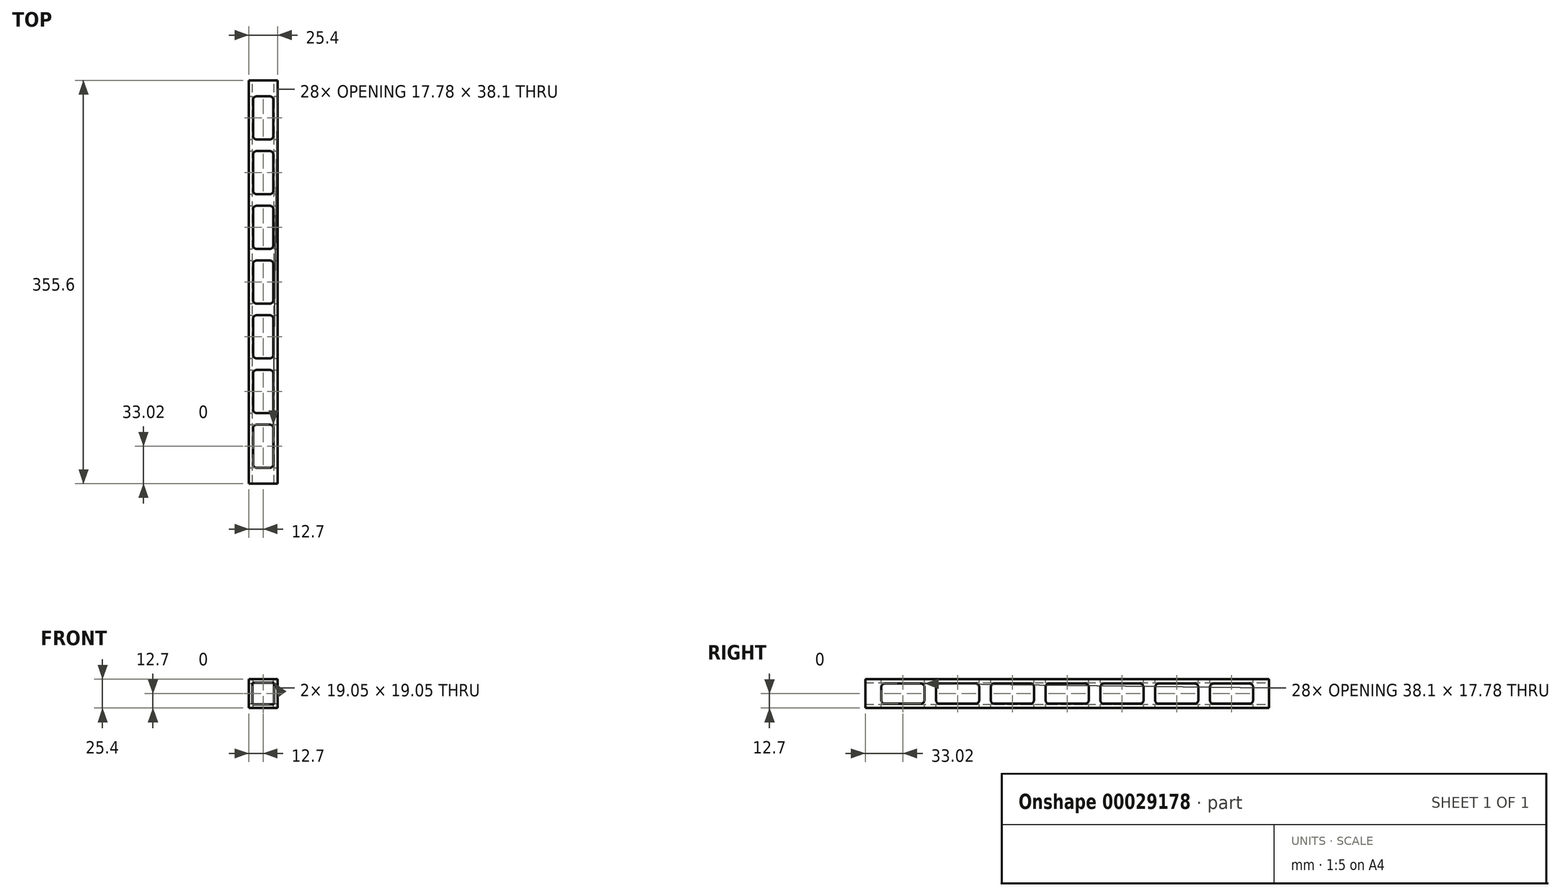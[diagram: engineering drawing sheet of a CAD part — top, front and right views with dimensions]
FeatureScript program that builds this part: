
annotation { "Feature Type Name" : "Feature", "Feature Type Description" : "" }
export const myFeature = defineFeature(function(context is Context, id is Id, definition is map)
    precondition{}
    {
        {
            var Q0;
            Q0=qCreatedBy(makeId("Front.planeOp"),FACE);
            var sketch = newSketch(context, id + "F0", { "sketchPlane" : qUnion([Q0])});
            skLineSegment(sketch, "E0.rect.bottom", {"start": v(12.7, 12.7) * mm, "end": v(-12.7, 12.7) * mm});
            skLineSegment(sketch, "E0.rect.top", {"start": v(12.7, -12.7) * mm, "end": v(-12.7, -12.7) * mm});
            skLineSegment(sketch, "E0.rect.left", {"start": v(12.7, 12.7) * mm, "end": v(12.7, -12.7) * mm});
            skLineSegment(sketch, "E0.rect.right", {"start": v(-12.7, 12.7) * mm, "end": v(-12.7, -12.7) * mm});
            skPoint(sketch, "E0.rect.middle", {"position": v(0, 0) * mm});
            skLineSegment(sketch, "E1.rect.bottom", {"start": v(9.53, 9.53) * mm, "end": v(-9.53, 9.53) * mm});
            skLineSegment(sketch, "E1.rect.top", {"start": v(9.53, -9.53) * mm, "end": v(-9.53, -9.53) * mm});
            skLineSegment(sketch, "E1.rect.left", {"start": v(9.53, 9.53) * mm, "end": v(9.53, -9.53) * mm});
            skLineSegment(sketch, "E1.rect.right", {"start": v(-9.53, 9.53) * mm, "end": v(-9.53, -9.53) * mm});
            skSolve(sketch);
        }
        {
            var Q0;
            Q0=qSketchRegion(id+"F0",true);
            extrude(context, id + "F1", {"entities" : qUnion([Q0]), "depth" : 355.6 * mm});
        }
        {
            var Q0;
            Q0=makeQuery(id+"F1.opExtrude","SWEPT_FACE",FACE,{"disambiguationData":[OSD([sQuery(id+"F0.wireOp",EDGE,"E0.rect.left")])]});
            var sketch = newSketch(context, id + "F2", { "sketchPlane" : qUnion([Q0])});
            skLineSegment(sketch, "E2", {"start": v(-355.6, 0) * mm, "end": v(-341.63, 0) * mm});
            skLineSegment(sketch, "E3.rect.bottom", {"start": v(-306.7, 8.89) * mm, "end": v(-338.46, 8.89) * mm});
            skLineSegment(sketch, "E3.rect.top", {"start": v(-306.7, -8.9) * mm, "end": v(-338.46, -8.9) * mm});
            skLineSegment(sketch, "E3.rect.left", {"start": v(-303.53, 5.71) * mm, "end": v(-303.53, -5.72) * mm});
            skLineSegment(sketch, "E3.rect.right", {"start": v(-341.63, 5.71) * mm, "end": v(-341.63, -5.72) * mm});
            skPoint(sketch, "E3.rect.middle", {"position": v(-322.58, 0) * mm});
            skPoint(sketch, "E4.visualSharp", {"position": v(-303.53, 8.89) * mm});
            skArc(sketch, "E4.filletArc", {"start": v(-303.53, 5.71) * mm, "mid": v(-304.46, 7.96) * mm, "end": v(-306.7, 8.89) * mm});
            skPoint(sketch, "E5.visualSharp", {"position": v(-303.53, -8.9) * mm});
            skArc(sketch, "E5.filletArc", {"start": v(-306.7, -8.9) * mm, "mid": v(-304.46, -7.96) * mm, "end": v(-303.53, -5.72) * mm});
            skPoint(sketch, "E6.visualSharp", {"position": v(-341.63, -8.9) * mm});
            skArc(sketch, "E6.filletArc", {"start": v(-341.63, -5.72) * mm, "mid": v(-340.7, -7.96) * mm, "end": v(-338.46, -8.9) * mm});
            skPoint(sketch, "E7.visualSharp", {"position": v(-341.63, 8.89) * mm});
            skArc(sketch, "E7.filletArc", {"start": v(-338.46, 8.89) * mm, "mid": v(-340.7, 7.96) * mm, "end": v(-341.63, 5.71) * mm});
            skLineSegment(sketch, "E8.1.0.0", {"start": v(-255.27, 5.71) * mm, "end": v(-255.27, -5.72) * mm});
            skArc(sketch, "E8.1.0.1", {"start": v(-255.27, 5.71) * mm, "mid": v(-256.2, 7.96) * mm, "end": v(-258.44, 8.89) * mm});
            skLineSegment(sketch, "E8.1.0.2", {"start": v(-258.44, 8.89) * mm, "end": v(-290.2, 8.89) * mm});
            skArc(sketch, "E8.1.0.3", {"start": v(-290.2, 8.89) * mm, "mid": v(-292.44, 7.96) * mm, "end": v(-293.37, 5.71) * mm});
            skLineSegment(sketch, "E8.1.0.4", {"start": v(-293.37, 5.71) * mm, "end": v(-293.37, -5.72) * mm});
            skArc(sketch, "E8.1.0.5", {"start": v(-293.37, -5.72) * mm, "mid": v(-292.44, -7.96) * mm, "end": v(-290.2, -8.9) * mm});
            skLineSegment(sketch, "E8.1.0.6", {"start": v(-258.44, -8.9) * mm, "end": v(-290.2, -8.9) * mm});
            skLineSegment(sketch, "E8.2.0.0", {"start": v(-207, 5.71) * mm, "end": v(-207, -5.72) * mm});
            skArc(sketch, "E8.2.0.1", {"start": v(-207, 5.71) * mm, "mid": v(-207.94, 7.96) * mm, "end": v(-210.18, 8.89) * mm});
            skLineSegment(sketch, "E8.2.0.2", {"start": v(-210.18, 8.89) * mm, "end": v(-241.94, 8.89) * mm});
            skArc(sketch, "E8.2.0.3", {"start": v(-241.94, 8.89) * mm, "mid": v(-244.18, 7.96) * mm, "end": v(-245.1, 5.71) * mm});
            skLineSegment(sketch, "E8.2.0.4", {"start": v(-245.1, 5.71) * mm, "end": v(-245.1, -5.72) * mm});
            skArc(sketch, "E8.2.0.5", {"start": v(-245.1, -5.72) * mm, "mid": v(-244.18, -7.96) * mm, "end": v(-241.94, -8.9) * mm});
            skLineSegment(sketch, "E8.2.0.6", {"start": v(-210.18, -8.9) * mm, "end": v(-241.94, -8.9) * mm});
            skLineSegment(sketch, "E8.3.0.0", {"start": v(-158.75, 5.71) * mm, "end": v(-158.75, -5.72) * mm});
            skArc(sketch, "E8.3.0.1", {"start": v(-158.75, 5.71) * mm, "mid": v(-159.68, 7.96) * mm, "end": v(-161.92, 8.89) * mm});
            skLineSegment(sketch, "E8.3.0.2", {"start": v(-161.92, 8.89) * mm, "end": v(-193.67, 8.89) * mm});
            skArc(sketch, "E8.3.0.3", {"start": v(-193.67, 8.89) * mm, "mid": v(-195.92, 7.96) * mm, "end": v(-196.85, 5.71) * mm});
            skLineSegment(sketch, "E8.3.0.4", {"start": v(-196.85, 5.71) * mm, "end": v(-196.85, -5.72) * mm});
            skArc(sketch, "E8.3.0.5", {"start": v(-196.85, -5.72) * mm, "mid": v(-195.92, -7.96) * mm, "end": v(-193.67, -8.9) * mm});
            skLineSegment(sketch, "E8.3.0.6", {"start": v(-161.92, -8.9) * mm, "end": v(-193.67, -8.9) * mm});
            skLineSegment(sketch, "E8.4.0.0", {"start": v(-110.49, 5.71) * mm, "end": v(-110.49, -5.72) * mm});
            skArc(sketch, "E8.4.0.1", {"start": v(-110.49, 5.71) * mm, "mid": v(-111.42, 7.96) * mm, "end": v(-113.66, 8.89) * mm});
            skLineSegment(sketch, "E8.4.0.2", {"start": v(-113.66, 8.89) * mm, "end": v(-145.41, 8.89) * mm});
            skArc(sketch, "E8.4.0.3", {"start": v(-145.41, 8.89) * mm, "mid": v(-147.66, 7.96) * mm, "end": v(-148.59, 5.71) * mm});
            skLineSegment(sketch, "E8.4.0.4", {"start": v(-148.59, 5.71) * mm, "end": v(-148.59, -5.72) * mm});
            skArc(sketch, "E8.4.0.5", {"start": v(-148.59, -5.72) * mm, "mid": v(-147.66, -7.96) * mm, "end": v(-145.41, -8.9) * mm});
            skLineSegment(sketch, "E8.4.0.6", {"start": v(-113.66, -8.9) * mm, "end": v(-145.41, -8.9) * mm});
            skLineSegment(sketch, "E8.5.0.0", {"start": v(-62.23, 5.71) * mm, "end": v(-62.23, -5.72) * mm});
            skArc(sketch, "E8.5.0.1", {"start": v(-62.23, 5.71) * mm, "mid": v(-63.16, 7.96) * mm, "end": v(-65.4, 8.89) * mm});
            skLineSegment(sketch, "E8.5.0.2", {"start": v(-65.4, 8.89) * mm, "end": v(-97.15, 8.89) * mm});
            skArc(sketch, "E8.5.0.3", {"start": v(-97.15, 8.89) * mm, "mid": v(-99.4, 7.96) * mm, "end": v(-100.33, 5.71) * mm});
            skLineSegment(sketch, "E8.5.0.4", {"start": v(-100.33, 5.71) * mm, "end": v(-100.33, -5.72) * mm});
            skArc(sketch, "E8.5.0.5", {"start": v(-100.33, -5.72) * mm, "mid": v(-99.4, -7.96) * mm, "end": v(-97.15, -8.9) * mm});
            skLineSegment(sketch, "E8.5.0.6", {"start": v(-65.4, -8.9) * mm, "end": v(-97.15, -8.9) * mm});
            skLineSegment(sketch, "E8.6.0.0", {"start": v(-13.97, 5.71) * mm, "end": v(-13.97, -5.72) * mm});
            skArc(sketch, "E8.6.0.1", {"start": v(-13.97, 5.71) * mm, "mid": v(-14.9, 7.96) * mm, "end": v(-17.14, 8.89) * mm});
            skLineSegment(sketch, "E8.6.0.2", {"start": v(-17.14, 8.89) * mm, "end": v(-48.9, 8.89) * mm});
            skArc(sketch, "E8.6.0.3", {"start": v(-48.9, 8.89) * mm, "mid": v(-51.14, 7.96) * mm, "end": v(-52.07, 5.71) * mm});
            skLineSegment(sketch, "E8.6.0.4", {"start": v(-52.07, 5.71) * mm, "end": v(-52.07, -5.72) * mm});
            skArc(sketch, "E8.6.0.5", {"start": v(-52.07, -5.72) * mm, "mid": v(-51.14, -7.96) * mm, "end": v(-48.9, -8.9) * mm});
            skLineSegment(sketch, "E8.6.0.6", {"start": v(-17.14, -8.9) * mm, "end": v(-48.9, -8.9) * mm});
            skLineSegment(sketch, "E8.direction1", {"start": v(-303.53, -5.72) * mm, "end": v(-255.27, -5.72) * mm, "construction": true});
            skLineSegment(sketch, "E9.trimOffspring", {"start": v(-303.53, 0) * mm, "end": v(-293.37, 0) * mm});
            skLineSegment(sketch, "E10.trimOffspring", {"start": v(-255.27, 0) * mm, "end": v(0, 0) * mm});
            skArc(sketch, "E11.1.0.0", {"start": v(-258.44, -8.9) * mm, "mid": v(-256.2, -7.96) * mm, "end": v(-255.27, -5.72) * mm});
            skArc(sketch, "E11.2.0.0", {"start": v(-210.18, -8.9) * mm, "mid": v(-207.94, -7.96) * mm, "end": v(-207, -5.72) * mm});
            skArc(sketch, "E11.3.0.0", {"start": v(-161.92, -8.9) * mm, "mid": v(-159.68, -7.96) * mm, "end": v(-158.75, -5.72) * mm});
            skArc(sketch, "E11.4.0.0", {"start": v(-113.66, -8.9) * mm, "mid": v(-111.42, -7.96) * mm, "end": v(-110.49, -5.72) * mm});
            skArc(sketch, "E11.5.0.0", {"start": v(-65.4, -8.9) * mm, "mid": v(-63.16, -7.96) * mm, "end": v(-62.23, -5.72) * mm});
            skArc(sketch, "E11.6.0.0", {"start": v(-17.14, -8.9) * mm, "mid": v(-14.9, -7.96) * mm, "end": v(-13.97, -5.72) * mm});
            skLineSegment(sketch, "E11.direction1", {"start": v(-306.7, -8.9) * mm, "end": v(-258.44, -8.9) * mm, "construction": true});
            skSolve(sketch);
        }
        {
            var Q0;
            Q0 = qSketchRegion(id + "F2", true);
            extrude(context, id + "F3", {"entities" : qUnion([Q0]), "operationType" : NewBodyOperationType.REMOVE, "oppositeDirection" : true, "depth" : 25.4 * mm});
        }
        {
            var Q0;
            Q0=makeQuery(id+"F1.opExtrude","SWEPT_FACE",FACE,{"disambiguationData":[OSD([sQuery(id+"F0.wireOp",EDGE,"E0.rect.bottom")])]});
            var sketch = newSketch(context, id + "F4", { "sketchPlane" : qUnion([Q0])});
            skLineSegment(sketch, "E12", {"start": v(0, -355.6) * mm, "end": v(0, -341.63) * mm});
            skLineSegment(sketch, "E13.rect.bottom", {"start": v(5.72, -303.53) * mm, "end": v(-5.71, -303.53) * mm});
            skLineSegment(sketch, "E13.rect.top", {"start": v(5.72, -341.63) * mm, "end": v(-5.71, -341.63) * mm});
            skLineSegment(sketch, "E13.rect.left", {"start": v(8.9, -306.7) * mm, "end": v(8.9, -338.46) * mm});
            skLineSegment(sketch, "E13.rect.right", {"start": v(-8.89, -306.7) * mm, "end": v(-8.89, -338.46) * mm});
            skPoint(sketch, "E13.rect.middle", {"position": v(0, -322.58) * mm});
            skPoint(sketch, "E14.visualSharp", {"position": v(-8.89, -303.53) * mm});
            skArc(sketch, "E14.filletArc", {"start": v(-5.71, -303.53) * mm, "mid": v(-7.96, -304.46) * mm, "end": v(-8.89, -306.7) * mm});
            skPoint(sketch, "E15.visualSharp", {"position": v(8.9, -303.53) * mm});
            skArc(sketch, "E15.filletArc", {"start": v(8.9, -306.7) * mm, "mid": v(7.96, -304.46) * mm, "end": v(5.72, -303.53) * mm});
            skPoint(sketch, "E16.visualSharp", {"position": v(8.9, -341.63) * mm});
            skArc(sketch, "E16.filletArc", {"start": v(5.72, -341.63) * mm, "mid": v(7.96, -340.7) * mm, "end": v(8.9, -338.46) * mm});
            skPoint(sketch, "E17.visualSharp", {"position": v(-8.89, -341.63) * mm});
            skArc(sketch, "E17.filletArc", {"start": v(-8.89, -338.46) * mm, "mid": v(-7.96, -340.7) * mm, "end": v(-5.71, -341.63) * mm});
            skLineSegment(sketch, "E18.trimOffspring", {"start": v(0, -303.53) * mm, "end": v(0, 0) * mm});
            skLineSegment(sketch, "E19.0.1.0", {"start": v(5.72, -255.27) * mm, "end": v(-5.71, -255.27) * mm});
            skArc(sketch, "E19.0.1.1", {"start": v(-5.71, -255.27) * mm, "mid": v(-7.96, -256.2) * mm, "end": v(-8.89, -258.44) * mm});
            skLineSegment(sketch, "E19.0.1.2", {"start": v(-8.89, -258.44) * mm, "end": v(-8.89, -290.2) * mm});
            skArc(sketch, "E19.0.1.3", {"start": v(-8.89, -290.2) * mm, "mid": v(-7.96, -292.44) * mm, "end": v(-5.71, -293.37) * mm});
            skLineSegment(sketch, "E19.0.1.4", {"start": v(5.72, -293.37) * mm, "end": v(-5.71, -293.37) * mm});
            skArc(sketch, "E19.0.1.5", {"start": v(5.72, -293.37) * mm, "mid": v(7.96, -292.44) * mm, "end": v(8.9, -290.2) * mm});
            skLineSegment(sketch, "E19.0.1.6", {"start": v(8.9, -258.44) * mm, "end": v(8.9, -290.2) * mm});
            skArc(sketch, "E19.0.1.7", {"start": v(8.9, -258.44) * mm, "mid": v(7.96, -256.2) * mm, "end": v(5.72, -255.27) * mm});
            skLineSegment(sketch, "E19.0.2.0", {"start": v(5.72, -207) * mm, "end": v(-5.71, -207) * mm});
            skArc(sketch, "E19.0.2.1", {"start": v(-5.71, -207) * mm, "mid": v(-7.96, -207.94) * mm, "end": v(-8.89, -210.18) * mm});
            skLineSegment(sketch, "E19.0.2.2", {"start": v(-8.89, -210.18) * mm, "end": v(-8.89, -241.94) * mm});
            skArc(sketch, "E19.0.2.3", {"start": v(-8.89, -241.94) * mm, "mid": v(-7.96, -244.18) * mm, "end": v(-5.71, -245.11) * mm});
            skLineSegment(sketch, "E19.0.2.4", {"start": v(5.72, -245.11) * mm, "end": v(-5.71, -245.11) * mm});
            skArc(sketch, "E19.0.2.5", {"start": v(5.72, -245.11) * mm, "mid": v(7.96, -244.18) * mm, "end": v(8.9, -241.94) * mm});
            skLineSegment(sketch, "E19.0.2.6", {"start": v(8.9, -210.18) * mm, "end": v(8.9, -241.94) * mm});
            skArc(sketch, "E19.0.2.7", {"start": v(8.9, -210.18) * mm, "mid": v(7.96, -207.94) * mm, "end": v(5.72, -207) * mm});
            skLineSegment(sketch, "E19.0.3.0", {"start": v(5.72, -158.75) * mm, "end": v(-5.71, -158.75) * mm});
            skArc(sketch, "E19.0.3.1", {"start": v(-5.71, -158.75) * mm, "mid": v(-7.96, -159.68) * mm, "end": v(-8.89, -161.92) * mm});
            skLineSegment(sketch, "E19.0.3.2", {"start": v(-8.89, -161.92) * mm, "end": v(-8.89, -193.68) * mm});
            skArc(sketch, "E19.0.3.3", {"start": v(-8.89, -193.68) * mm, "mid": v(-7.96, -195.92) * mm, "end": v(-5.71, -196.85) * mm});
            skLineSegment(sketch, "E19.0.3.4", {"start": v(5.72, -196.85) * mm, "end": v(-5.71, -196.85) * mm});
            skArc(sketch, "E19.0.3.5", {"start": v(5.72, -196.85) * mm, "mid": v(7.96, -195.92) * mm, "end": v(8.9, -193.68) * mm});
            skLineSegment(sketch, "E19.0.3.6", {"start": v(8.9, -161.92) * mm, "end": v(8.9, -193.68) * mm});
            skArc(sketch, "E19.0.3.7", {"start": v(8.9, -161.92) * mm, "mid": v(7.96, -159.68) * mm, "end": v(5.72, -158.75) * mm});
            skLineSegment(sketch, "E19.0.4.0", {"start": v(5.72, -110.49) * mm, "end": v(-5.71, -110.49) * mm});
            skArc(sketch, "E19.0.4.1", {"start": v(-5.71, -110.49) * mm, "mid": v(-7.96, -111.42) * mm, "end": v(-8.89, -113.66) * mm});
            skLineSegment(sketch, "E19.0.4.2", {"start": v(-8.89, -113.66) * mm, "end": v(-8.89, -145.42) * mm});
            skArc(sketch, "E19.0.4.3", {"start": v(-8.89, -145.42) * mm, "mid": v(-7.96, -147.66) * mm, "end": v(-5.71, -148.6) * mm});
            skLineSegment(sketch, "E19.0.4.4", {"start": v(5.72, -148.6) * mm, "end": v(-5.71, -148.6) * mm});
            skArc(sketch, "E19.0.4.5", {"start": v(5.72, -148.6) * mm, "mid": v(7.96, -147.66) * mm, "end": v(8.9, -145.42) * mm});
            skLineSegment(sketch, "E19.0.4.6", {"start": v(8.9, -113.66) * mm, "end": v(8.9, -145.42) * mm});
            skArc(sketch, "E19.0.4.7", {"start": v(8.9, -113.66) * mm, "mid": v(7.96, -111.42) * mm, "end": v(5.72, -110.49) * mm});
            skLineSegment(sketch, "E19.0.5.0", {"start": v(5.72, -62.23) * mm, "end": v(-5.71, -62.23) * mm});
            skArc(sketch, "E19.0.5.1", {"start": v(-5.71, -62.23) * mm, "mid": v(-7.96, -63.16) * mm, "end": v(-8.89, -65.4) * mm});
            skLineSegment(sketch, "E19.0.5.2", {"start": v(-8.89, -65.4) * mm, "end": v(-8.89, -97.15) * mm});
            skArc(sketch, "E19.0.5.3", {"start": v(-8.89, -97.15) * mm, "mid": v(-7.96, -99.4) * mm, "end": v(-5.71, -100.33) * mm});
            skLineSegment(sketch, "E19.0.5.4", {"start": v(5.72, -100.33) * mm, "end": v(-5.71, -100.33) * mm});
            skArc(sketch, "E19.0.5.5", {"start": v(5.72, -100.33) * mm, "mid": v(7.96, -99.4) * mm, "end": v(8.9, -97.15) * mm});
            skLineSegment(sketch, "E19.0.5.6", {"start": v(8.9, -65.4) * mm, "end": v(8.9, -97.15) * mm});
            skArc(sketch, "E19.0.5.7", {"start": v(8.9, -65.4) * mm, "mid": v(7.96, -63.16) * mm, "end": v(5.72, -62.23) * mm});
            skLineSegment(sketch, "E19.0.6.0", {"start": v(5.71, -13.97) * mm, "end": v(-5.72, -13.97) * mm});
            skArc(sketch, "E19.0.6.1", {"start": v(-5.72, -13.97) * mm, "mid": v(-7.96, -14.9) * mm, "end": v(-8.89, -17.14) * mm});
            skLineSegment(sketch, "E19.0.6.2", {"start": v(-8.89, -17.14) * mm, "end": v(-8.89, -48.9) * mm});
            skArc(sketch, "E19.0.6.3", {"start": v(-8.89, -48.9) * mm, "mid": v(-7.96, -51.14) * mm, "end": v(-5.72, -52.07) * mm});
            skLineSegment(sketch, "E19.0.6.4", {"start": v(5.71, -52.07) * mm, "end": v(-5.72, -52.07) * mm});
            skArc(sketch, "E19.0.6.5", {"start": v(5.71, -52.07) * mm, "mid": v(7.96, -51.14) * mm, "end": v(8.9, -48.9) * mm});
            skLineSegment(sketch, "E19.0.6.6", {"start": v(8.9, -17.14) * mm, "end": v(8.9, -48.9) * mm});
            skArc(sketch, "E19.0.6.7", {"start": v(8.9, -17.14) * mm, "mid": v(7.96, -14.9) * mm, "end": v(5.71, -13.97) * mm});
            skLineSegment(sketch, "E19.direction1", {"start": v(-5.71, -303.53) * mm, "end": v(19.69, -303.53) * mm, "construction": true});
            skLineSegment(sketch, "E19.direction2", {"start": v(-5.71, -303.53) * mm, "end": v(-5.71, -255.27) * mm, "construction": true});
            skSolve(sketch);
        }
        {
            var Q0;
            Q0 = qSketchRegion(id + "F4", true);
            extrude(context, id + "F5", {"entities" : qUnion([Q0]), "operationType" : NewBodyOperationType.REMOVE, "oppositeDirection" : true, "depth" : 25.4 * mm});
        }
    });
